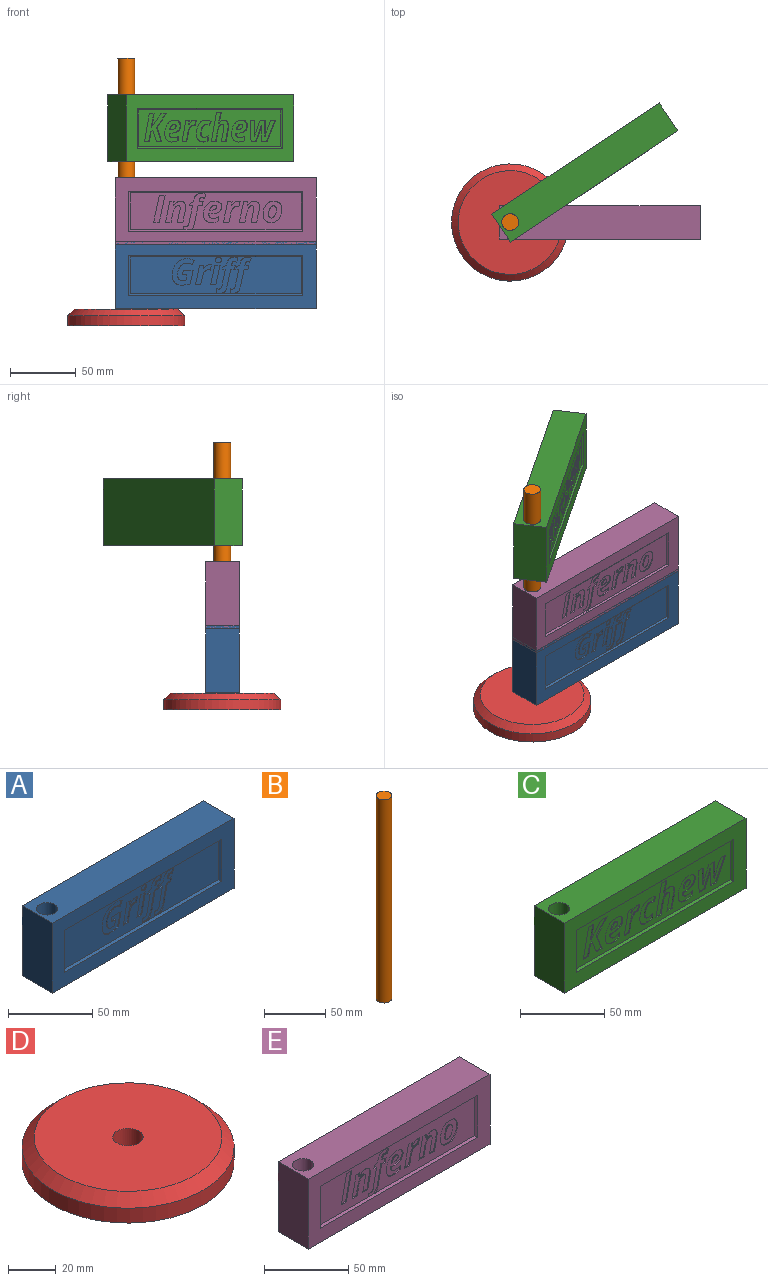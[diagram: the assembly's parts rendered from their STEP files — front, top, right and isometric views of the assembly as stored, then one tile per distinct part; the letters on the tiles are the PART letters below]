
ASSEMBLY  parts=5 mates=6
PART A: 109 faces, bbox 152.4x25.4x50.8 mm
  f0: plane 129.54x27.94mm, normal (0,-1,0), area 3011.8mm2, adj f8,f9,f10,f11,f12,f13,f14,f15
  f1: plane 152.4x50.8mm, normal (0,-1,0), area 3716.1mm2, adj f2,f3,f4,f5,f8,f9,f10,f11
  f2: plane 50.8x25.4mm, normal (1,0,0), area 1290.3mm2, adj f1,f3,f5,f6
  f3: plane 152.4x25.4mm, normal (0,0,1), area 3744.3mm2, adj f1,f2,f4,f6,f7
  f4: plane 50.8x25.4mm, normal (-1,0,0), area 1290.3mm2, adj f1,f3,f5,f6
  f5: plane 152.4x25.4mm, normal (0,0,-1), area 3744.3mm2, adj f1,f2,f4,f6,f7
  f6: plane 152.4x50.8mm, normal (0,1,0), area 7741.9mm2, adj f2,f3,f4,f5
  f7: cylinder r=6.35mm len=50.8mm, axis (0,0,1), area 2026.8mm2, adj f3,f5
  f8: plane 30.48x1.27mm, normal (0.71,-0.71,0), area 52.5mm2, adj f0,f1,f9,f10
  f9: plane 132.08x1.27mm, normal (0,-0.71,-0.71), area 234.9mm2, adj f0,f1,f8,f11
  f10: plane 132.08x1.27mm, normal (0,-0.71,0.71), area 234.9mm2, adj f0,f1,f8,f11
  f11: plane 30.48x1.27mm, normal (-0.71,-0.71,0), area 52.5mm2, adj f0,f1,f9,f10
  f12: plane 4.01x0.76mm, normal (0,0,1), area 3.1mm2, adj f0,f13,f15,f16
  f13: plane 14.89x3.16mm, normal (-0.98,0,0.21), area 11.6mm2, adj f0,f12,f14,f16
  f14: plane 4.01x0.76mm, normal (0,0,-1), area 3.1mm2, adj f0,f13,f15,f16
  f15: plane 14.89x3.15mm, normal (0.98,0,-0.21), area 11.6mm2, adj f0,f12,f14,f16
  f16: plane 14.89x7.16mm, normal (0,-1,0), area 59.7mm2, adj f12,f13,f14,f15
  f17: extruded ~2.31x0.76mm, area 1.8mm2, adj f0,f18,f39,f40
  f18: extruded ~5.37x4.94mm, area 6.1mm2, adj f0,f17,f19,f40
  f19: plane 13.45x2.86mm, normal (-0.98,0,0.21), area 10.5mm2, adj f0,f18,f20,f40
  f20: plane 2.93x0.76mm, normal (0,0,1), area 2.2mm2, adj f0,f19,f21,f40
  f21: plane 3.05x0.76mm, normal (-0.98,0,0.21), area 2.4mm2, adj f0,f20,f22,f40
  f22: plane 2.91x0.76mm, normal (0,0,-1), area 2.2mm2, adj f0,f21,f23,f40
  f23: plane 0.83x0.76mm, normal (-0.98,0,0.19), area 0.6mm2, adj f0,f22,f24,f40
  f24: extruded ~1.4x0.76mm, area 1.2mm2, adj f0,f23,f25,f40
  f25: extruded ~1.23x0.76mm, area 1.1mm2, adj f0,f24,f26,f40
  f26: extruded ~1.77x0.76mm, area 1.4mm2, adj f0,f25,f27,f40
  f27: plane 2.98x1.07mm, normal (-0.94,0,0.34), area 2.4mm2, adj f0,f26,f28,f40
  f28: extruded ~3.13x0.76mm, area 2.5mm2, adj f0,f27,f29,f40
  f29: extruded ~3.64x1.17mm, area 3mm2, adj f0,f28,f30,f40
  f30: extruded ~3.7x1.84mm, area 3.2mm2, adj f0,f29,f31,f40
  f31: plane 1.12x0.76mm, normal (0.98,0,-0.21), area 0.9mm2, adj f0,f30,f32,f40
  f32: plane 2.44x1.12mm, normal (0.42,0,-0.91), area 2mm2, adj f0,f31,f33,f40
  f33: plane 1.93x0.76mm, normal (0.98,0,-0.2), area 1.5mm2, adj f0,f32,f34,f40
  f34: plane 2.17x0.76mm, normal (0,0,1), area 1.7mm2, adj f0,f33,f35,f40
  f35: plane 12.85x2.71mm, normal (0.98,0,-0.21), area 10mm2, adj f0,f34,f36,f40
  f36: extruded ~1.73x0.87mm, area 1.5mm2, adj f0,f35,f37,f40
  f37: extruded ~1.43x0.76mm, area 1.2mm2, adj f0,f36,f38,f40
  f38: extruded ~1.53x0.76mm, area 1.2mm2, adj f0,f37,f39,f40
  f39: plane 3.22x0.76mm, normal (1,0,0), area 2.5mm2, adj f0,f17,f38,f40
  f40: plane 27.42x16.06mm, normal (0,-1,0), area 139mm2, adj f17,f18,f19,f20,f21,f22,f23,f24
  f41: extruded ~1.75x0.76mm, area 1.5mm2, adj f0,f42,f47,f48
  f42: extruded ~2.01x1.64mm, area 2.3mm2, adj f0,f41,f43,f48
  f43: extruded ~1.81x0.76mm, area 1.5mm2, adj f0,f42,f44,f48
  f44: extruded ~1.73x0.76mm, area 1.4mm2, adj f0,f43,f45,f48
  f45: extruded ~1.18x0.76mm, area 1mm2, adj f0,f44,f46,f48
  f46: extruded ~1.48x0.76mm, area 1.2mm2, adj f0,f45,f47,f48
  f47: extruded ~1.79x0.76mm, area 1.5mm2, adj f0,f41,f46,f48
  f48: plane 4.41x3.98mm, normal (0,-1,0), area 14.5mm2, adj f41,f42,f43,f44,f45,f46,f47
  f49: extruded ~1.28x0.76mm, area 1mm2, adj f0,f50,f60,f61
  f50: extruded ~4.7x3.03mm, area 4.5mm2, adj f0,f49,f51,f61
  f51: plane 0.76x0.08mm, normal (0,0,-1), area 0.1mm2, adj f0,f50,f52,f61
  f52: plane 2.76x0.76mm, normal (-0.99,0,0.1), area 2.1mm2, adj f0,f51,f53,f61
  f53: plane 3.06x0.76mm, normal (0,0,-1), area 2.3mm2, adj f0,f52,f54,f61
  f54: plane 14.89x3.15mm, normal (0.98,0,-0.21), area 11.6mm2, adj f0,f53,f55,f61
  f55: plane 4.01x0.76mm, normal (0,0,1), area 3.1mm2, adj f0,f54,f56,f61
  f56: plane 6.66x1.41mm, normal (-0.98,0,0.21), area 5.2mm2, adj f0,f55,f57,f61
  f57: extruded ~3.49x1.66mm, area 3mm2, adj f0,f56,f58,f61
  f58: extruded ~2.71x1.22mm, area 2.3mm2, adj f0,f57,f59,f61
  f59: extruded ~1.33x0.76mm, area 1mm2, adj f0,f58,f60,f61
  f60: plane 3.86x0.88mm, normal (-0.98,0,0.22), area 3mm2, adj f0,f49,f59,f61
  f61: plane 15.17x11.99mm, normal (0,-1,0), area 76.9mm2, adj f49,f50,f51,f52,f53,f54,f55,f56
  f62: extruded ~2.31x0.76mm, area 1.8mm2, adj f0,f63,f84,f85
  f63: extruded ~5.37x4.94mm, area 6.1mm2, adj f0,f62,f64,f85
  f64: plane 13.45x2.86mm, normal (-0.98,0,0.21), area 10.5mm2, adj f0,f63,f65,f85
  f65: plane 2.93x0.76mm, normal (0,0,1), area 2.2mm2, adj f0,f64,f66,f85
  f66: plane 3.05x0.76mm, normal (-0.98,0,0.21), area 2.4mm2, adj f0,f65,f67,f85
  f67: plane 2.91x0.76mm, normal (0,0,-1), area 2.2mm2, adj f0,f66,f68,f85
  f68: plane 0.83x0.76mm, normal (-0.98,0,0.19), area 0.6mm2, adj f0,f67,f69,f85
  f69: extruded ~1.4x0.76mm, area 1.2mm2, adj f0,f68,f70,f85
  f70: extruded ~1.23x0.76mm, area 1.1mm2, adj f0,f69,f71,f85
  f71: extruded ~1.77x0.76mm, area 1.4mm2, adj f0,f70,f72,f85
  f72: plane 2.98x1.07mm, normal (-0.94,0,0.34), area 2.4mm2, adj f0,f71,f73,f85
  f73: extruded ~3.13x0.76mm, area 2.5mm2, adj f0,f72,f74,f85
  f74: extruded ~3.64x1.17mm, area 3mm2, adj f0,f73,f75,f85
  f75: extruded ~3.7x1.84mm, area 3.2mm2, adj f0,f74,f76,f85
  f76: plane 1.12x0.76mm, normal (0.98,0,-0.21), area 0.9mm2, adj f0,f75,f77,f85
  f77: plane 2.44x1.12mm, normal (0.42,0,-0.91), area 2mm2, adj f0,f76,f78,f85
  f78: plane 1.93x0.76mm, normal (0.98,0,-0.2), area 1.5mm2, adj f0,f77,f79,f85
  f79: plane 2.17x0.76mm, normal (0,0,1), area 1.7mm2, adj f0,f78,f80,f85
  f80: plane 12.85x2.71mm, normal (0.98,0,-0.21), area 10mm2, adj f0,f79,f81,f85
  f81: extruded ~1.73x0.87mm, area 1.5mm2, adj f0,f80,f82,f85
  f82: extruded ~1.43x0.76mm, area 1.2mm2, adj f0,f81,f83,f85
  f83: extruded ~1.53x0.76mm, area 1.2mm2, adj f0,f82,f84,f85
  f84: plane 3.22x0.76mm, normal (1,0,0), area 2.5mm2, adj f0,f62,f83,f85
  f85: plane 27.42x16.06mm, normal (0,-1,0), area 139mm2, adj f62,f63,f64,f65,f66,f67,f68,f69
  f86: plane 7.5x0.76mm, normal (0,0,-1), area 5.7mm2, adj f0,f87,f107,f108
  f87: plane 3.44x0.76mm, normal (0.98,0,-0.21), area 2.7mm2, adj f0,f86,f88,f108
  f88: plane 3.56x0.76mm, normal (0,0,1), area 2.7mm2, adj f0,f87,f89,f108
  f89: plane 3.98x0.88mm, normal (0.98,0,-0.22), area 3.1mm2, adj f0,f88,f90,f108
  f90: extruded ~2.26x0.76mm, area 1.7mm2, adj f0,f89,f91,f108
  f91: extruded ~2.96x1.07mm, area 2.5mm2, adj f0,f90,f92,f108
  f92: extruded ~3.36x0.97mm, area 2.7mm2, adj f0,f91,f93,f108
  f93: extruded ~4.4x0.91mm, area 3.4mm2, adj f0,f92,f94,f108
  f94: extruded ~3.15x2.52mm, area 3.1mm2, adj f0,f93,f95,f108
  f95: extruded ~3.64x1.11mm, area 2.9mm2, adj f0,f94,f96,f108
  f96: extruded ~2.14x0.76mm, area 1.7mm2, adj f0,f95,f97,f108
  f97: extruded ~1.97x0.85mm, area 1.6mm2, adj f0,f96,f98,f108
  f98: plane 3.34x1.53mm, normal (-0.91,0,0.42), area 2.8mm2, adj f0,f97,f99,f108
  f99: extruded ~5.46x1.32mm, area 4.3mm2, adj f0,f98,f100,f108
  f100: extruded ~5.96x1.57mm, area 4.8mm2, adj f0,f99,f101,f108
  f101: extruded ~4.45x4.01mm, area 4.6mm2, adj f0,f100,f102,f108
  f102: extruded ~6.45x1.43mm, area 5.1mm2, adj f0,f101,f103,f108
  f103: extruded ~5.62x1.88mm, area 4.6mm2, adj f0,f102,f104,f108
  f104: extruded ~5.33x1.96mm, area 4.4mm2, adj f0,f103,f105,f108
  f105: extruded ~3.23x0.76mm, area 2.5mm2, adj f0,f104,f106,f108
  f106: extruded ~3.31x0.83mm, area 2.6mm2, adj f0,f105,f107,f108
  f107: plane 10.15x2.16mm, normal (-0.98,0,0.21), area 7.9mm2, adj f0,f86,f106,f108
  f108: plane 20.04x16.86mm, normal (0,-1,0), area 178.5mm2, adj f86,f87,f88,f89,f90,f91,f92,f93
PART B: 3 faces, bbox 12.7x12.7x203.2 mm
  f0: cylinder r=6.35mm len=203.2mm, axis (0,0,-1), area 8107.3mm2, adj f1,f2
  f1: plane 12.7x12.7mm, normal (0,0,1), area 126.7mm2, adj f0
  f2: plane 12.7x12.7mm, normal (0,0,-1), area 126.7mm2, adj f0
PART C: 157 faces, bbox 152.4x25.4x50.8 mm
  f0: plane 129.54x27.94mm, normal (0,-1,0), area 2509.1mm2, adj f8,f9,f10,f11,f12,f13,f14,f15
  f1: plane 152.4x50.8mm, normal (0,-1,0), area 3716.1mm2, adj f2,f3,f4,f5,f8,f9,f10,f11
  f2: plane 50.8x25.4mm, normal (1,0,0), area 1290.3mm2, adj f1,f3,f5,f6
  f3: plane 152.4x25.4mm, normal (0,0,1), area 3744.3mm2, adj f1,f2,f4,f6,f7
  f4: plane 50.8x25.4mm, normal (-1,0,0), area 1290.3mm2, adj f1,f3,f5,f6
  f5: plane 152.4x25.4mm, normal (0,0,-1), area 3744.3mm2, adj f1,f2,f4,f6,f7
  f6: plane 152.4x50.8mm, normal (0,1,0), area 7741.9mm2, adj f2,f3,f4,f5
  f7: cylinder r=6.35mm len=50.8mm, axis (0,0,1), area 2026.8mm2, adj f3,f5
  f8: plane 30.48x1.27mm, normal (0.71,-0.71,0), area 52.5mm2, adj f0,f1,f9,f10
  f9: plane 132.08x1.27mm, normal (0,-0.71,-0.71), area 234.9mm2, adj f0,f1,f8,f11
  f10: plane 132.08x1.27mm, normal (0,-0.71,0.71), area 234.9mm2, adj f0,f1,f8,f11
  f11: plane 30.48x1.27mm, normal (-0.71,-0.71,0), area 52.5mm2, adj f0,f1,f9,f10
  f12: plane 4.87x0.76mm, normal (0,0,1), area 3.7mm2, adj f0,f13,f24,f25
  f13: plane 10.97x4.19mm, normal (-0.93,0,-0.36), area 8.9mm2, adj f0,f12,f14,f25
  f14: plane 10.08x8.55mm, normal (-0.76,0,0.65), area 10.1mm2, adj f0,f13,f15,f25
  f15: plane 5.2x0.76mm, normal (0,0,-1), area 4mm2, adj f0,f14,f16,f25
  f16: plane 7.15x5.89mm, normal (0.77,0,-0.64), area 7.1mm2, adj f0,f15,f17,f25
  f17: plane 2.95x2.27mm, normal (0.79,0,-0.61), area 2.8mm2, adj f0,f16,f18,f25
  f18: plane 10.11x2.19mm, normal (-0.98,0,0.21), area 7.9mm2, adj f0,f17,f19,f25
  f19: plane 4.41x0.76mm, normal (0,0,-1), area 3.4mm2, adj f0,f18,f20,f25
  f20: plane 21.05x4.45mm, normal (0.98,0,-0.21), area 16.4mm2, adj f0,f19,f21,f25
  f21: plane 4.39x0.76mm, normal (0,0,1), area 3.3mm2, adj f0,f20,f22,f25
  f22: plane 7.51x1.57mm, normal (-0.98,0,0.2), area 5.8mm2, adj f0,f21,f23,f25
  f23: plane 1.8x1.01mm, normal (-0.49,0,0.87), area 1.6mm2, adj f0,f22,f24,f25
  f24: plane 8.52x3.04mm, normal (0.94,0,0.34), area 6.9mm2, adj f0,f12,f23,f25
  f25: plane 21.05x20.02mm, normal (0,-1,0), area 197.8mm2, adj f12,f13,f14,f15,f16,f17,f18,f19
  f26: extruded ~4.7x1.63mm, area 3.9mm2, adj f0,f27,f49,f50
  f27: extruded ~5.61x1.24mm, area 4.4mm2, adj f0,f26,f28,f50
  f28: plane 3.27x0.76mm, normal (-1,0,0), area 2.5mm2, adj f0,f27,f29,f50
  f29: extruded ~2.47x0.97mm, area 2mm2, adj f0,f28,f30,f50
  f30: extruded ~2.28x0.76mm, area 1.8mm2, adj f0,f29,f31,f50
  f31: extruded ~2.12x0.76mm, area 1.8mm2, adj f0,f30,f32,f50
  f32: extruded ~2.06x0.76mm, area 1.7mm2, adj f0,f31,f33,f50
  f33: plane 0.76x0.29mm, normal (-1,0,0), area 0.2mm2, adj f0,f32,f34,f50
  f34: plane 0.76x0.3mm, normal (-1,0,0.09), area 0.2mm2, adj f0,f33,f35,f50
  f35: plane 0.76x0.74mm, normal (0,0,1), area 0.6mm2, adj f0,f34,f36,f50
  f36: extruded ~6.87x1.46mm, area 5.4mm2, adj f0,f35,f37,f50
  f37: extruded ~4.15x2.4mm, area 3.8mm2, adj f0,f36,f38,f50
  f38: extruded ~3.22x1.42mm, area 2.8mm2, adj f0,f37,f39,f50
  f39: extruded ~3.98x1.17mm, area 3.2mm2, adj f0,f38,f40,f50
  f40: extruded ~4.59x1.29mm, area 3.7mm2, adj f0,f39,f41,f50
  f41: extruded ~3.74x3.22mm, area 3.8mm2, adj f0,f40,f42,f50
  f42: extruded ~5.43x1.19mm, area 4.3mm2, adj f0,f41,f49,f50
  f43: extruded ~2.39x1.15mm, area 2.1mm2, adj f44,f48,f50,f51
  f44: extruded ~1.51x1.37mm, area 1.8mm2, adj f43,f45,f50,f51
  f45: extruded ~1.89x1.24mm, area 1.8mm2, adj f44,f46,f50,f51
  f46: extruded ~3.48x0.76mm, area 2.7mm2, adj f45,f47,f50,f51
  f47: plane 0.76x0.65mm, normal (0,0,-1), area 0.5mm2, adj f46,f48,f50,f51
  f48: extruded ~2.81x1.47mm, area 2.4mm2, adj f43,f47,f50,f51
  f49: extruded ~4.59x1.67mm, area 3.8mm2, adj f0,f26,f42,f50
  f50: plane 16.68x14.39mm, normal (0,-1,0), area 145.3mm2, adj f26,f27,f28,f29,f30,f31,f32,f33
  f51: plane 5.37x3.96mm, normal (0,-1,0), area 14.5mm2, adj f43,f44,f45,f46,f47,f48
  f52: extruded ~4.7x1.63mm, area 3.9mm2, adj f0,f53,f75,f76
  f53: extruded ~5.61x1.24mm, area 4.4mm2, adj f0,f52,f54,f76
  f54: plane 3.27x0.76mm, normal (-1,0,0), area 2.5mm2, adj f0,f53,f55,f76
  f55: extruded ~2.47x0.97mm, area 2mm2, adj f0,f54,f56,f76
  f56: extruded ~2.28x0.76mm, area 1.8mm2, adj f0,f55,f57,f76
  f57: extruded ~2.12x0.76mm, area 1.8mm2, adj f0,f56,f58,f76
  f58: extruded ~2.06x0.76mm, area 1.7mm2, adj f0,f57,f59,f76
  f59: plane 0.76x0.29mm, normal (-1,0,0), area 0.2mm2, adj f0,f58,f60,f76
  f60: plane 0.76x0.3mm, normal (-1,0,0.09), area 0.2mm2, adj f0,f59,f61,f76
  f61: plane 0.76x0.74mm, normal (0,0,1), area 0.6mm2, adj f0,f60,f62,f76
  f62: extruded ~6.87x1.46mm, area 5.4mm2, adj f0,f61,f63,f76
  f63: extruded ~4.15x2.4mm, area 3.8mm2, adj f0,f62,f64,f76
  f64: extruded ~3.22x1.42mm, area 2.8mm2, adj f0,f63,f65,f76
  f65: extruded ~3.98x1.17mm, area 3.2mm2, adj f0,f64,f66,f76
  f66: extruded ~4.59x1.29mm, area 3.7mm2, adj f0,f65,f67,f76
  f67: extruded ~3.74x3.22mm, area 3.8mm2, adj f0,f66,f68,f76
  f68: extruded ~5.43x1.19mm, area 4.3mm2, adj f0,f67,f75,f76
  f69: extruded ~2.39x1.15mm, area 2.1mm2, adj f70,f74,f76,f77
  f70: extruded ~1.51x1.37mm, area 1.8mm2, adj f69,f71,f76,f77
  f71: extruded ~1.89x1.24mm, area 1.8mm2, adj f70,f72,f76,f77
  f72: extruded ~3.48x0.76mm, area 2.7mm2, adj f71,f73,f76,f77
  f73: plane 0.76x0.65mm, normal (0,0,-1), area 0.5mm2, adj f72,f74,f76,f77
  f74: extruded ~2.81x1.47mm, area 2.4mm2, adj f69,f73,f76,f77
  f75: extruded ~4.59x1.67mm, area 3.8mm2, adj f0,f52,f68,f76
  f76: plane 16.68x14.39mm, normal (0,-1,0), area 145.3mm2, adj f52,f53,f54,f55,f56,f57,f58,f59
  f77: plane 5.37x3.96mm, normal (0,-1,0), area 14.5mm2, adj f69,f70,f71,f72,f73,f74
  f78: extruded ~4.59x1.77mm, area 3.8mm2, adj f0,f79,f103,f104
  f79: plane 0.76x0.09mm, normal (0,0,1), area 0.1mm2, adj f0,f78,f80,f104
  f80: extruded ~4.9x0.76mm, area 3.7mm2, adj f0,f79,f81,f104
  f81: plane 7.49x0.76mm, normal (1,0,0.01), area 5.7mm2, adj f0,f80,f82,f104
  f82: plane 4.75x0.76mm, normal (0,0,1), area 3.6mm2, adj f0,f81,f83,f104
  f83: plane 16.09x7.63mm, normal (-0.9,0,0.43), area 13.6mm2, adj f0,f82,f84,f104
  f84: plane 4.42x0.76mm, normal (0,0,-1), area 3.4mm2, adj f0,f83,f85,f104
  f85: plane 7.13x3.15mm, normal (0.91,0,-0.4), area 5.9mm2, adj f0,f84,f86,f104
  f86: extruded ~3.71x1.37mm, area 3mm2, adj f0,f85,f87,f104
  f87: plane 1.15x0.76mm, normal (0.94,0,-0.33), area 0.9mm2, adj f0,f86,f88,f104
  f88: plane 0.76x0.09mm, normal (0,0,-1), area 0.1mm2, adj f0,f87,f89,f104
  f89: extruded ~4.27x0.76mm, area 3.3mm2, adj f0,f88,f90,f104
  f90: plane 7.72x0.76mm, normal (-1,0,0), area 5.9mm2, adj f0,f89,f91,f104
  f91: plane 4.72x0.76mm, normal (0,0,-1), area 3.6mm2, adj f0,f90,f92,f104
  f92: plane 7.72x3.33mm, normal (0.92,0,-0.4), area 6.4mm2, adj f0,f91,f93,f104
  f93: extruded ~1.71x0.76mm, area 1.4mm2, adj f0,f92,f94,f104
  f94: extruded ~1.96x0.76mm, area 1.6mm2, adj f0,f93,f95,f104
  f95: extruded ~0.76x0.6mm, area 0.5mm2, adj f0,f94,f96,f104
  f96: plane 0.76x0.06mm, normal (0,0,-1), area 0mm2, adj f0,f95,f97,f104
  f97: plane 2.46x0.76mm, normal (-1,0,0.04), area 1.9mm2, adj f0,f96,f98,f104
  f98: plane 2.4x0.76mm, normal (-1,0,0.02), area 1.8mm2, adj f0,f97,f99,f104
  f99: plane 7.13x0.76mm, normal (-1,0,-0.01), area 5.4mm2, adj f0,f98,f100,f104
  f100: plane 4.04x0.76mm, normal (0,0,-1), area 3.1mm2, adj f0,f99,f101,f104
  f101: plane 16.09x0.76mm, normal (1,0,0.05), area 12.3mm2, adj f0,f100,f102,f104
  f102: plane 4.67x0.76mm, normal (0,0,1), area 3.6mm2, adj f0,f101,f103,f104
  f103: plane 7.79x3.35mm, normal (-0.92,0,0.4), area 6.5mm2, adj f0,f78,f102,f104
  f104: plane 22.93x16.09mm, normal (0,-1,0), area 215.7mm2, adj f78,f79,f80,f81,f82,f83,f84,f85
  f105: plane 4.33x0.76mm, normal (0,0,1), area 3.3mm2, adj f0,f106,f123,f124
  f106: plane 9.17x1.92mm, normal (-0.98,0,0.2), area 7.1mm2, adj f0,f105,f107,f124
  f107: extruded ~2.59x0.76mm, area 2mm2, adj f0,f106,f108,f124
  f108: extruded ~3.43x1.09mm, area 2.8mm2, adj f0,f107,f109,f124
  f109: extruded ~3.07x1.2mm, area 2.6mm2, adj f0,f108,f110,f124
  f110: extruded ~2.54x0.76mm, area 2mm2, adj f0,f109,f111,f124
  f111: extruded ~1.99x1.78mm, area 2mm2, adj f0,f110,f112,f124
  f112: plane 0.76x0.12mm, normal (0,0,-1), area 0.1mm2, adj f0,f111,f113,f124
  f113: extruded ~4.45x1.24mm, area 3.5mm2, adj f0,f112,f114,f124
  f114: extruded ~4x0.87mm, area 3.1mm2, adj f0,f113,f115,f124
  f115: plane 4.33x0.76mm, normal (0,0,-1), area 3.3mm2, adj f0,f114,f116,f124
  f116: plane 22.4x4.75mm, normal (0.98,0,-0.21), area 17.4mm2, adj f0,f115,f117,f124
  f117: plane 4.33x0.76mm, normal (0,0,1), area 3.3mm2, adj f0,f116,f118,f124
  f118: plane 6.67x1.41mm, normal (-0.98,0,0.21), area 5.2mm2, adj f0,f117,f119,f124
  f119: extruded ~4.58x1.7mm, area 3.7mm2, adj f0,f118,f120,f124
  f120: extruded ~2.4x1.64mm, area 2.3mm2, adj f0,f119,f121,f124
  f121: extruded ~1.77x1.56mm, area 2.1mm2, adj f0,f120,f122,f124
  f122: extruded ~1.71x0.76mm, area 1.3mm2, adj f0,f121,f123,f124
  f123: plane 9.4x1.97mm, normal (0.98,0,-0.21), area 7.3mm2, adj f0,f105,f122,f124
  f124: plane 22.4x15.78mm, normal (0,-1,0), area 179.3mm2, adj f105,f106,f107,f108,f109,f110,f111,f112
  f125: extruded ~4.44x1.55mm, area 3.7mm2, adj f0,f126,f142,f143
  f126: extruded ~4.84x1.14mm, area 3.8mm2, adj f0,f125,f127,f143
  f127: plane 3.54x0.76mm, normal (-1,0,0), area 2.7mm2, adj f0,f126,f128,f143
  f128: extruded ~1.93x0.84mm, area 1.6mm2, adj f0,f127,f129,f143
  f129: extruded ~2.03x0.76mm, area 1.6mm2, adj f0,f128,f130,f143
  f130: extruded ~1.82x0.76mm, area 1.5mm2, adj f0,f129,f131,f143
  f131: extruded ~2.08x0.76mm, area 1.7mm2, adj f0,f130,f132,f143
  f132: extruded ~3.45x0.76mm, area 2.7mm2, adj f0,f131,f133,f143
  f133: extruded ~2.53x1.54mm, area 2.3mm2, adj f0,f132,f134,f143
  f134: extruded ~2.21x0.92mm, area 1.9mm2, adj f0,f133,f135,f143
  f135: extruded ~1.7x0.76mm, area 1.3mm2, adj f0,f134,f136,f143
  f136: extruded ~1.53x0.76mm, area 1.2mm2, adj f0,f135,f137,f143
  f137: plane 3.29x1.32mm, normal (-0.93,0,0.37), area 2.7mm2, adj f0,f136,f138,f143
  f138: extruded ~4.72x1.04mm, area 3.7mm2, adj f0,f137,f139,f143
  f139: extruded ~4.43x1.36mm, area 3.6mm2, adj f0,f138,f140,f143
  f140: extruded ~3.86x3.02mm, area 3.8mm2, adj f0,f139,f141,f143
  f141: extruded ~5.55x1.07mm, area 4.3mm2, adj f0,f140,f142,f143
  f142: extruded ~4.37x1.55mm, area 3.6mm2, adj f0,f125,f141,f143
  f143: plane 16.68x13.24mm, normal (0,-1,0), area 108mm2, adj f125,f126,f127,f128,f129,f130,f131,f132
  f144: extruded ~1.38x0.76mm, area 1.1mm2, adj f0,f145,f155,f156
  f145: extruded ~5.08x3.28mm, area 4.8mm2, adj f0,f144,f146,f156
  f146: plane 0.76x0.09mm, normal (0,0,-1), area 0.1mm2, adj f0,f145,f147,f156
  f147: plane 2.98x0.76mm, normal (-0.99,0,0.1), area 2.3mm2, adj f0,f146,f148,f156
  f148: plane 3.31x0.76mm, normal (0,0,-1), area 2.5mm2, adj f0,f147,f149,f156
  f149: plane 16.09x3.41mm, normal (0.98,0,-0.21), area 12.5mm2, adj f0,f148,f150,f156
  f150: plane 4.33x0.76mm, normal (0,0,1), area 3.3mm2, adj f0,f149,f151,f156
  f151: plane 7.2x1.53mm, normal (-0.98,0,0.21), area 5.6mm2, adj f0,f150,f152,f156
  f152: extruded ~3.78x1.79mm, area 3.2mm2, adj f0,f151,f153,f156
  f153: extruded ~2.93x1.32mm, area 2.5mm2, adj f0,f152,f154,f156
  f154: extruded ~1.44x0.76mm, area 1.1mm2, adj f0,f153,f155,f156
  f155: plane 4.17x0.95mm, normal (-0.98,0,0.22), area 3.3mm2, adj f0,f144,f154,f156
  f156: plane 16.39x12.97mm, normal (0,-1,0), area 89.8mm2, adj f144,f145,f146,f147,f148,f149,f150,f151
PART D: 6 faces, bbox 88.9x88.9x12.7 mm
  f0: cylinder r=44.45mm len=88.9mm, axis (0,0,-1), area 2128.2mm2, adj f2,f3
  f1: plane 78.74x78.74mm, normal (0,0,1), area 4742.8mm2, adj f3,f4
  f2: plane 88.9x88.9mm, normal (0,0,-1), area 6207.2mm2, adj f0
  f3: cone r=39.37mm half-angle=45deg, axis (0,0,-1), area 1891.8mm2, adj f0,f1
  f4: cylinder r=6.35mm len=12.7mm, axis (0,0,1), area 505.7mm2, adj f1,f5
  f5: plane 12.7x12.7mm, normal (0,0,1), area 126.7mm2, adj f4
PART E: 137 faces, bbox 152.4x25.4x50.8 mm
  f0: plane 129.54x28.09mm, normal (0,-1,0), area 2679.9mm2, adj f8,f9,f10,f11,f12,f13,f14,f15
  f1: plane 152.4x50.8mm, normal (0,-1,0), area 3716.1mm2, adj f2,f3,f4,f5,f8,f9,f10,f11
  f2: plane 50.8x25.4mm, normal (1,0,0), area 1290.3mm2, adj f1,f3,f5,f6
  f3: plane 152.4x25.4mm, normal (0,0,1), area 3744.3mm2, adj f1,f2,f4,f6,f7
  f4: plane 50.8x25.4mm, normal (-1,0,0), area 1290.3mm2, adj f1,f3,f5,f6
  f5: plane 152.4x25.4mm, normal (0,0,-1), area 3744.3mm2, adj f1,f2,f4,f6,f7
  f6: plane 152.4x50.8mm, normal (0,1,0), area 7741.9mm2, adj f2,f3,f4,f5
  f7: cylinder r=6.35mm len=50.8mm, axis (0,0,1), area 2026.8mm2, adj f3,f5
  f8: plane 30.48x1.27mm, normal (0.71,-0.71,0), area 52.5mm2, adj f0,f1,f9,f10
  f9: plane 132.08x1.27mm, normal (0,-0.71,-0.71), area 234.9mm2, adj f0,f1,f8,f11
  f10: plane 132.08x1.27mm, normal (0,-0.71,0.71), area 234.9mm2, adj f0,f1,f8,f11,f131
  f11: plane 30.48x1.27mm, normal (-0.71,-0.71,0), area 52.5mm2, adj f0,f1,f9,f10
  f12: extruded ~4.56x1.58mm, area 3.8mm2, adj f0,f13,f35,f36
  f13: extruded ~5.45x1.2mm, area 4.3mm2, adj f0,f12,f14,f36
  f14: plane 3.18x0.76mm, normal (-1,0,0), area 2.4mm2, adj f0,f13,f15,f36
  f15: extruded ~2.4x0.94mm, area 2mm2, adj f0,f14,f16,f36
  f16: extruded ~2.21x0.76mm, area 1.7mm2, adj f0,f15,f17,f36
  f17: extruded ~2.06x0.76mm, area 1.7mm2, adj f0,f16,f18,f36
  f18: extruded ~2x0.76mm, area 1.7mm2, adj f0,f17,f19,f36
  f19: plane 0.76x0.28mm, normal (-1,0,0), area 0.2mm2, adj f0,f18,f20,f36
  f20: plane 0.76x0.3mm, normal (-1,0,0.09), area 0.2mm2, adj f0,f19,f21,f36
  f21: plane 0.76x0.72mm, normal (0,0,1), area 0.5mm2, adj f0,f20,f22,f36
  f22: extruded ~6.67x1.42mm, area 5.3mm2, adj f0,f21,f23,f36
  f23: extruded ~4.03x2.33mm, area 3.7mm2, adj f0,f22,f24,f36
  f24: extruded ~3.13x1.38mm, area 2.7mm2, adj f0,f23,f25,f36
  f25: extruded ~3.86x1.14mm, area 3.1mm2, adj f0,f24,f26,f36
  f26: extruded ~4.46x1.25mm, area 3.6mm2, adj f0,f25,f27,f36
  f27: extruded ~3.64x3.13mm, area 3.7mm2, adj f0,f26,f28,f36
  f28: extruded ~5.28x1.15mm, area 4.2mm2, adj f0,f27,f35,f36
  f29: extruded ~2.32x1.12mm, area 2mm2, adj f30,f34,f36,f37
  f30: extruded ~1.47x1.33mm, area 1.7mm2, adj f29,f31,f36,f37
  f31: extruded ~1.84x1.21mm, area 1.8mm2, adj f30,f32,f36,f37
  f32: extruded ~3.38x0.76mm, area 2.7mm2, adj f31,f33,f36,f37
  f33: plane 0.76x0.63mm, normal (0,0,-1), area 0.5mm2, adj f32,f34,f36,f37
  f34: extruded ~2.73x1.43mm, area 2.4mm2, adj f29,f33,f36,f37
  f35: extruded ~4.46x1.62mm, area 3.7mm2, adj f0,f12,f28,f36
  f36: plane 16.21x13.98mm, normal (0,-1,0), area 137.1mm2, adj f12,f13,f14,f15,f16,f17,f18,f19
  f37: plane 5.21x3.84mm, normal (0,-1,0), area 13.7mm2, adj f29,f30,f31,f32,f33,f34
  f38: plane 4.21x0.76mm, normal (0,0,1), area 3.2mm2, adj f0,f39,f54,f55
  f39: plane 8.91x1.86mm, normal (-0.98,0,0.2), area 6.9mm2, adj f0,f38,f40,f55
  f40: extruded ~2.51x0.76mm, area 1.9mm2, adj f0,f39,f41,f55
  f41: extruded ~3.34x1.06mm, area 2.7mm2, adj f0,f40,f42,f55
  f42: extruded ~2.98x1.17mm, area 2.5mm2, adj f0,f41,f43,f55
  f43: extruded ~4.97x3.19mm, area 4.7mm2, adj f0,f42,f44,f55
  f44: plane 0.76x0.09mm, normal (0,0,-1), area 0.1mm2, adj f0,f43,f45,f55
  f45: plane 2.9x0.76mm, normal (-0.99,0,0.1), area 2.2mm2, adj f0,f44,f46,f55
  f46: plane 3.22x0.76mm, normal (0,0,-1), area 2.5mm2, adj f0,f45,f47,f55
  f47: plane 15.63x3.31mm, normal (0.98,0,-0.21), area 12.2mm2, adj f0,f46,f48,f55
  f48: plane 4.21x0.76mm, normal (0,0,1), area 3.2mm2, adj f0,f47,f49,f55
  f49: plane 6.48x1.37mm, normal (-0.98,0,0.21), area 5mm2, adj f0,f48,f50,f55
  f50: extruded ~4.45x1.65mm, area 3.6mm2, adj f0,f49,f51,f55
  f51: extruded ~2.33x1.6mm, area 2.2mm2, adj f0,f50,f52,f55
  f52: extruded ~1.72x1.51mm, area 2mm2, adj f0,f51,f53,f55
  f53: extruded ~1.66x0.76mm, area 1.3mm2, adj f0,f52,f54,f55
  f54: plane 9.13x1.92mm, normal (0.98,0,-0.21), area 7.1mm2, adj f0,f38,f53,f55
  f55: plane 15.93x15.33mm, normal (0,-1,0), area 142mm2, adj f38,f39,f40,f41,f42,f43,f44,f45
  f56: extruded ~1.34x0.76mm, area 1mm2, adj f0,f57,f67,f68
  f57: extruded ~4.94x3.19mm, area 4.7mm2, adj f0,f56,f58,f68
  f58: plane 0.76x0.09mm, normal (0,0,-1), area 0.1mm2, adj f0,f57,f59,f68
  f59: plane 2.9x0.76mm, normal (-0.99,0,0.1), area 2.2mm2, adj f0,f58,f60,f68
  f60: plane 3.22x0.76mm, normal (0,0,-1), area 2.5mm2, adj f0,f59,f61,f68
  f61: plane 15.63x3.31mm, normal (0.98,0,-0.21), area 12.2mm2, adj f0,f60,f62,f68
  f62: plane 4.21x0.76mm, normal (0,0,1), area 3.2mm2, adj f0,f61,f63,f68
  f63: plane 6.99x1.49mm, normal (-0.98,0,0.21), area 5.4mm2, adj f0,f62,f64,f68
  f64: extruded ~3.67x1.74mm, area 3.1mm2, adj f0,f63,f65,f68
  f65: extruded ~2.85x1.28mm, area 2.4mm2, adj f0,f64,f66,f68
  f66: extruded ~1.4x0.76mm, area 1.1mm2, adj f0,f65,f67,f68
  f67: plane 4.05x0.92mm, normal (-0.98,0,0.22), area 3.2mm2, adj f0,f56,f66,f68
  f68: plane 15.93x12.6mm, normal (0,-1,0), area 84.8mm2, adj f56,f57,f58,f59,f60,f61,f62,f63
  f69: plane 4.21x0.76mm, normal (0,0,1), area 3.2mm2, adj f0,f70,f85,f86
  f70: plane 8.91x1.86mm, normal (-0.98,0,0.2), area 6.9mm2, adj f0,f69,f71,f86
  f71: extruded ~2.51x0.76mm, area 1.9mm2, adj f0,f70,f72,f86
  f72: extruded ~3.34x1.06mm, area 2.7mm2, adj f0,f71,f73,f86
  f73: extruded ~2.98x1.17mm, area 2.5mm2, adj f0,f72,f74,f86
  f74: extruded ~4.97x3.19mm, area 4.7mm2, adj f0,f73,f75,f86
  f75: plane 0.76x0.09mm, normal (0,0,-1), area 0.1mm2, adj f0,f74,f76,f86
  f76: plane 2.9x0.76mm, normal (-0.99,0,0.1), area 2.2mm2, adj f0,f75,f77,f86
  f77: plane 3.22x0.76mm, normal (0,0,-1), area 2.5mm2, adj f0,f76,f78,f86
  f78: plane 15.63x3.31mm, normal (0.98,0,-0.21), area 12.2mm2, adj f0,f77,f79,f86
  f79: plane 4.21x0.76mm, normal (0,0,1), area 3.2mm2, adj f0,f78,f80,f86
  f80: plane 6.48x1.37mm, normal (-0.98,0,0.21), area 5mm2, adj f0,f79,f81,f86
  f81: extruded ~4.45x1.65mm, area 3.6mm2, adj f0,f80,f82,f86
  f82: extruded ~2.33x1.6mm, area 2.2mm2, adj f0,f81,f83,f86
  f83: extruded ~1.72x1.51mm, area 2mm2, adj f0,f82,f84,f86
  f84: extruded ~1.66x0.76mm, area 1.3mm2, adj f0,f83,f85,f86
  f85: plane 9.13x1.92mm, normal (0.98,0,-0.21), area 7.1mm2, adj f0,f69,f84,f86
  f86: plane 15.93x15.33mm, normal (0,-1,0), area 142mm2, adj f69,f70,f71,f72,f73,f74,f75,f76
  f87: extruded ~5.23x0.99mm, area 4.1mm2, adj f0,f88,f104,f105
  f88: extruded ~4.54x1.6mm, area 3.8mm2, adj f0,f87,f89,f105
  f89: extruded ~4.33x1.65mm, area 3.6mm2, adj f0,f88,f90,f105
  f90: extruded ~4.42x1.28mm, area 3.6mm2, adj f0,f89,f91,f105
  f91: extruded ~3.61x2.89mm, area 3.6mm2, adj f0,f90,f92,f105
  f92: extruded ~5.31x1mm, area 4.1mm2, adj f0,f91,f93,f105
  f93: extruded ~4.37x1.63mm, area 3.7mm2, adj f0,f92,f94,f105
  f94: extruded ~4.36x1.64mm, area 3.6mm2, adj f0,f93,f95,f105
  f95: extruded ~4.42x1.25mm, area 3.6mm2, adj f0,f94,f104,f105
  f96: extruded ~2.76x2mm, area 3mm2, adj f97,f103,f105,f106
  f97: extruded ~3.33x0.76mm, area 2.6mm2, adj f96,f98,f105,f106
  f98: extruded ~2.39x1.31mm, area 2.1mm2, adj f97,f99,f105,f106
  f99: extruded ~1.89x0.86mm, area 1.6mm2, adj f98,f100,f105,f106
  f100: extruded ~2.59x2.1mm, area 2.9mm2, adj f99,f101,f105,f106
  f101: extruded ~3.4x0.76mm, area 2.6mm2, adj f100,f102,f105,f106
  f102: extruded ~2.5x1.36mm, area 2.2mm2, adj f101,f103,f105,f106
  f103: extruded ~1.88x0.85mm, area 1.6mm2, adj f96,f102,f105,f106
  f104: extruded ~3.53x2.85mm, area 3.5mm2, adj f0,f87,f95,f105
  f105: plane 16.21x14.24mm, normal (0,-1,0), area 143.7mm2, adj f87,f88,f89,f90,f91,f92,f93,f94
  f106: plane 9.34x5.76mm, normal (0,-1,0), area 41.7mm2, adj f96,f97,f98,f99,f100,f101,f102,f103
  f107: plane 3.38x0.76mm, normal (1,0,0), area 2.6mm2, adj f0,f108,f129,f130,f131
  f108: extruded ~2.43x0.76mm, area 1.9mm2, adj f107,f109,f130,f131
  f109: extruded ~5.64x5.19mm, area 6.4mm2, adj f0,f108,f110,f130,f131
  f110: plane 14.12x3.01mm, normal (-0.98,0,0.21), area 11mm2, adj f0,f109,f111,f130
  f111: plane 3.07x0.76mm, normal (0,0,1), area 2.3mm2, adj f0,f110,f112,f130
  f112: plane 3.2x0.76mm, normal (-0.98,0,0.21), area 2.5mm2, adj f0,f111,f113,f130
  f113: plane 3.06x0.76mm, normal (0,0,-1), area 2.3mm2, adj f0,f112,f114,f130
  f114: plane 0.87x0.76mm, normal (-0.98,0,0.19), area 0.7mm2, adj f0,f113,f115,f130
  f115: extruded ~1.47x0.76mm, area 1.2mm2, adj f0,f114,f116,f130
  f116: extruded ~1.29x0.76mm, area 1.1mm2, adj f0,f115,f117,f130
  f117: extruded ~1.86x0.76mm, area 1.5mm2, adj f0,f116,f118,f130
  f118: plane 3.13x1.12mm, normal (-0.94,0,0.34), area 2.5mm2, adj f0,f117,f119,f130
  f119: extruded ~3.28x0.76mm, area 2.6mm2, adj f0,f118,f120,f130
  f120: extruded ~3.82x1.22mm, area 3.1mm2, adj f0,f119,f121,f130
  f121: extruded ~3.88x1.94mm, area 3.4mm2, adj f0,f120,f122,f130
  f122: plane 1.17x0.76mm, normal (0.98,0,-0.21), area 0.9mm2, adj f0,f121,f123,f130
  f123: plane 2.56x1.18mm, normal (0.42,0,-0.91), area 2.1mm2, adj f0,f122,f124,f130
  f124: plane 2.03x0.76mm, normal (0.98,0,-0.2), area 1.6mm2, adj f0,f123,f125,f130
  f125: plane 2.28x0.76mm, normal (0,0,1), area 1.7mm2, adj f0,f124,f126,f130
  f126: plane 13.5x2.85mm, normal (0.98,0,-0.21), area 10.5mm2, adj f0,f125,f127,f130
  f127: extruded ~1.82x0.91mm, area 1.6mm2, adj f0,f126,f128,f130
  f128: extruded ~1.5x0.76mm, area 1.2mm2, adj f0,f127,f129,f130
  f129: extruded ~1.61x0.76mm, area 1.3mm2, adj f0,f107,f128,f130
  f130: plane 28.79x16.86mm, normal (0,-1,0), area 153.3mm2, adj f107,f108,f109,f110,f111,f112,f113,f114
  f131: plane 6.2x1.38mm, normal (0,1,0), area 5.9mm2, adj f10,f107,f108,f109
  f132: plane 20.45x4.36mm, normal (0.98,0,-0.21), area 15.9mm2, adj f0,f133,f135,f136
  f133: plane 4.26x0.76mm, normal (0,0,1), area 3.2mm2, adj f0,f132,f134,f136
  f134: plane 20.45x4.36mm, normal (-0.98,0,0.21), area 15.9mm2, adj f0,f133,f135,f136
  f135: plane 4.26x0.76mm, normal (0,0,-1), area 3.2mm2, adj f0,f132,f134,f136
  f136: plane 20.45x8.63mm, normal (0,-1,0), area 87.2mm2, adj f132,f133,f134,f135
PLACE A rot(axis=(1,0,0),0deg) t=(67.98,0,25.66)mm
PLACE B rot(axis=(1,0,0),180deg) t=(0,0,88.93)mm
PLACE C rot(axis=(0,0,1),33.6deg) t=(56.59,37.67,137.21)mm
PLACE D rot(axis=(1,0,0),0deg) t=(0,0,-12.7)mm
PLACE E rot(axis=(1,0,0),0deg) t=(67.98,0,74.35)mm
MATE slider B.f0 <-> E.f7  axis (0,0,1) through (0,0,190.53)mm
MATE cylindrical E.f7 <-> B.f0  axis (0,0,1) through (0,0,99.75)mm
MATE slider B.f0 <-> A.f7  axis (0,0,1) through (0,0,88.93)mm
MATE fastened B.f0 <-> D.f4  axis (0,0,-1) through (0,0,-12.67)mm
MATE cylindrical A.f7 <-> B.f0  axis (0,0,1) through (0,0,51.06)mm
MATE cylindrical C.f7 <-> B.f0  axis (0,0,1) through (0,0,162.61)mm
